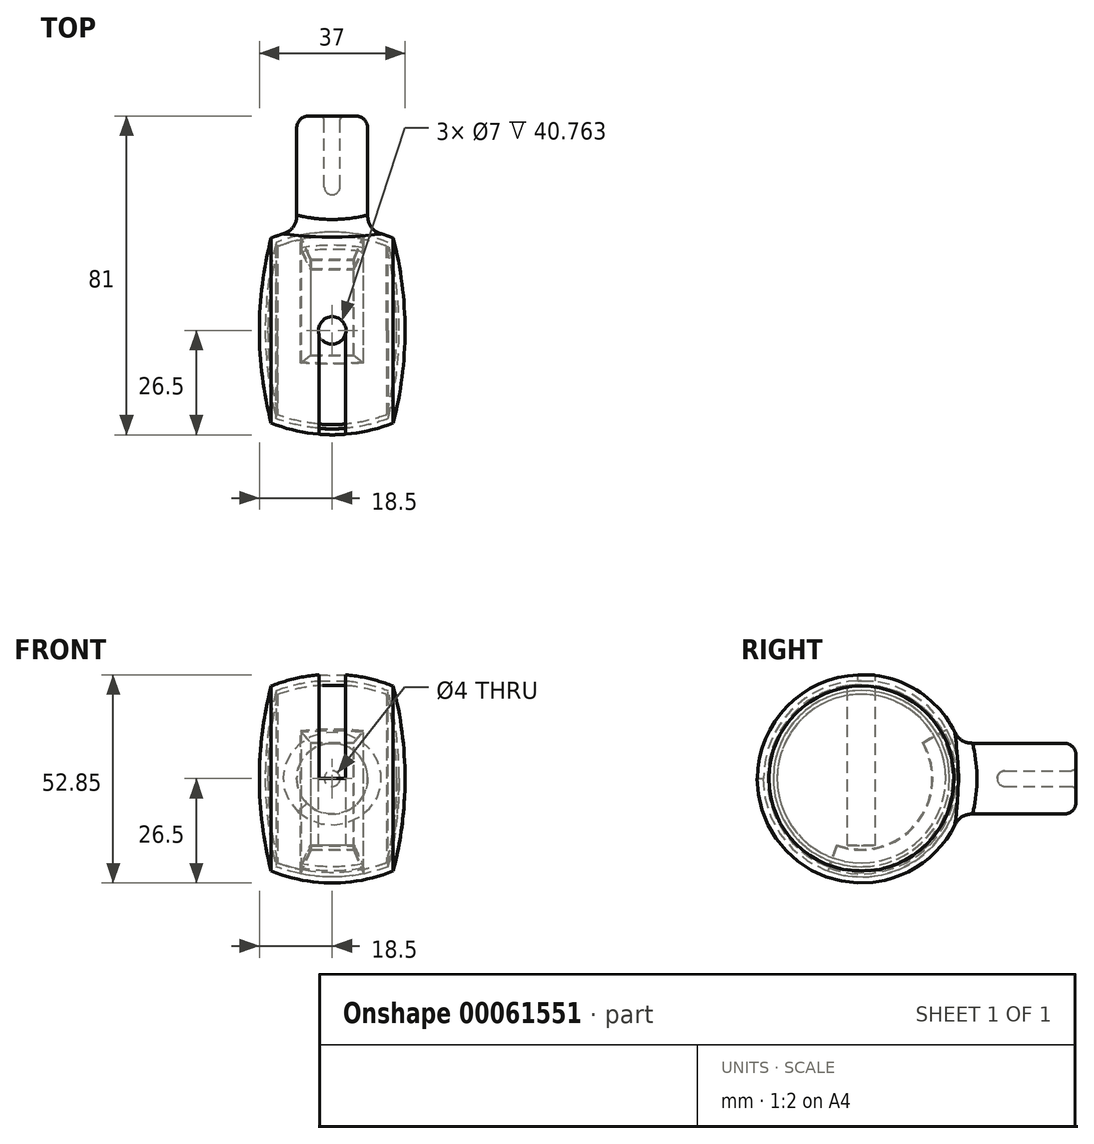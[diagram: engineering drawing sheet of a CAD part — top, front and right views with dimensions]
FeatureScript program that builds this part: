
annotation { "Feature Type Name" : "Feature", "Feature Type Description" : "" }
export const myFeature = defineFeature(function(context is Context, id is Id, definition is map)
    precondition{}
    {
        {
            var Q0;
            Q0=qCreatedBy(makeId("Front.planeOp"),FACE);
            var sketch = newSketch(context, id + "F0", { "sketchPlane" : qUnion([Q0])});
            skLineSegment(sketch, "E0.rect.bottom", {"start": v(18.5, -26.5) * mm, "end": v(-18.5, -26.5) * mm, "construction": true});
            skLineSegment(sketch, "E0.rect.top", {"start": v(18.5, 26.5) * mm, "end": v(-18.5, 26.5) * mm, "construction": true});
            skLineSegment(sketch, "E0.rect.left", {"start": v(18.5, -26.5) * mm, "end": v(18.5, 26.5) * mm, "construction": true});
            skLineSegment(sketch, "E0.rect.right", {"start": v(-18.5, -26.5) * mm, "end": v(-18.5, 26.5) * mm, "construction": true});
            skPoint(sketch, "E0.rect.middle", {"position": v(0, 0) * mm});
            skLineSegment(sketch, "E1.0", {"start": v(15.5, 23.5) * mm, "end": v(-15.5, 23.5) * mm, "construction": true});
            skLineSegment(sketch, "E1.1", {"start": v(15.5, -23.5) * mm, "end": v(15.5, 23.5) * mm, "construction": true});
            skLineSegment(sketch, "E1.2", {"start": v(15.5, -23.5) * mm, "end": v(-15.5, -23.5) * mm, "construction": true});
            skLineSegment(sketch, "E1.3", {"start": v(-15.5, -23.5) * mm, "end": v(-15.5, 23.5) * mm, "construction": true});
            skLineSegment(sketch, "E2", {"start": v(-87, 0) * mm, "end": v(88.34, 0) * mm, "construction": true});
            skArc(sketch, "E3", {"start": v(15.5, 23.5) * mm, "mid": v(0, 26.5) * mm, "end": v(-15.5, 23.5) * mm});
            skArc(sketch, "E4", {"start": v(-15.5, 23.5) * mm, "mid": v(-17.75, 11.85) * mm, "end": v(-18.5, 0) * mm});
            skLineSegment(sketch, "E5", {"start": v(0, 52.42) * mm, "end": v(0, -50.98) * mm, "construction": true});
            skPoint(sketch, "E5.endSnap0", {"position": v(0, -26.5) * mm});
            skArc(sketch, "E6.MirrorCS", {"start": v(15.5, 23.5) * mm, "mid": v(17.75, 11.85) * mm, "end": v(18.5, 0) * mm});
            skPoint(sketch, "E7.orphan", {"position": v(15.5, -23.5) * mm});
            skPoint(sketch, "E8.MirrorCS.center.orphan", {"position": v(0, 30.4) * mm});
            skPoint(sketch, "E8.MirrorCS.end.orphan", {"position": v(-15.5, -23.5) * mm});
            skArc(sketch, "E9.0", {"start": v(-14.24, 22.38) * mm, "mid": v(-16.3, 11.28) * mm, "end": v(-17, 0) * mm});
            skArc(sketch, "E9.1", {"start": v(14.24, 22.38) * mm, "mid": v(0, 25) * mm, "end": v(-14.24, 22.38) * mm});
            skArc(sketch, "E9.2", {"start": v(14.24, 22.38) * mm, "mid": v(16.3, 11.28) * mm, "end": v(17, 0) * mm});
            skLineSegment(sketch, "E10", {"start": v(-18.5, 0) * mm, "end": v(-17, 0) * mm});
            skLineSegment(sketch, "E11", {"start": v(17, 0) * mm, "end": v(18.5, 0) * mm});
            skLineSegment(sketch, "E12", {"start": v(-8.02, 24.19) * mm, "end": v(-5.41, 18.14) * mm});
            skLineSegment(sketch, "E13", {"start": v(-5.41, 18.14) * mm, "end": v(5.41, 18.14) * mm});
            skLineSegment(sketch, "E14", {"start": v(5.41, 18.14) * mm, "end": v(8.02, 24.19) * mm});
            skSolve(sketch);
        }
        {
            var Q0;
            {var subQ0=sQuery(id+"F0.wireOp",EDGE,"E12");Q0=makeQuery(id+"F0.imprint","IMPRINT",FACE,{"disambiguationData":[TD([[makeQuery(id+"F0.imprint","IMPRINT",EDGE,{"derivedFrom":subQ0}),1.0]])]});}
            var Q1;
            Q1=sQuery(id+"F0.wireOp",EDGE,"E2");
            revolve(context, id + "F1", {"entities" : qUnion([Q0]), "axis" : qUnion([Q1]), "revolveType" : RevolveType.ONE_DIRECTION, "oppositeDirection" : true, "angle" : 140 * degree});
        }
        {
            var Q0;
            Q0=qCreatedBy(makeId("Front.planeOp"),FACE);
            var sketch = newSketch(context, id + "F2", { "sketchPlane" : qUnion([Q0])});
            skLineSegment(sketch, "E15.rect.bottom", {"start": v(18.5, -26.5) * mm, "end": v(-18.5, -26.5) * mm, "construction": true});
            skLineSegment(sketch, "E15.rect.top", {"start": v(18.5, 26.5) * mm, "end": v(-18.5, 26.5) * mm, "construction": true});
            skLineSegment(sketch, "E15.rect.left", {"start": v(18.5, -26.5) * mm, "end": v(18.5, 26.5) * mm, "construction": true});
            skLineSegment(sketch, "E15.rect.right", {"start": v(-18.5, -26.5) * mm, "end": v(-18.5, 26.5) * mm, "construction": true});
            skPoint(sketch, "E15.rect.middle", {"position": v(0, 0) * mm});
            skLineSegment(sketch, "E16.0", {"start": v(15.5, 23.5) * mm, "end": v(-15.5, 23.5) * mm, "construction": true});
            skLineSegment(sketch, "E16.1", {"start": v(15.5, -23.5) * mm, "end": v(15.5, 23.5) * mm, "construction": true});
            skLineSegment(sketch, "E16.2", {"start": v(15.5, -23.5) * mm, "end": v(-15.5, -23.5) * mm, "construction": true});
            skLineSegment(sketch, "E16.3", {"start": v(-15.5, -23.5) * mm, "end": v(-15.5, 23.5) * mm, "construction": true});
            skLineSegment(sketch, "E17", {"start": v(-52.75, 0) * mm, "end": v(55.66, 0) * mm, "construction": true});
            skArc(sketch, "E18", {"start": v(15.5, 23.5) * mm, "mid": v(0, 26.5) * mm, "end": v(-15.5, 23.5) * mm});
            skArc(sketch, "E19", {"start": v(-15.5, 23.5) * mm, "mid": v(-17.75, 11.85) * mm, "end": v(-18.5, 0) * mm});
            skLineSegment(sketch, "E20", {"start": v(0, 37.06) * mm, "end": v(0, -36.72) * mm, "construction": true});
            skPoint(sketch, "E20.endSnap0", {"position": v(0, -26.5) * mm});
            skArc(sketch, "E21.MirrorCS", {"start": v(15.5, 23.5) * mm, "mid": v(17.75, 11.85) * mm, "end": v(18.5, 0) * mm});
            skPoint(sketch, "E22.orphan", {"position": v(15.5, -23.5) * mm});
            skPoint(sketch, "E23.MirrorCS.center.orphan", {"position": v(0, 15.04) * mm});
            skPoint(sketch, "E23.MirrorCS.end.orphan", {"position": v(-15.5, -23.5) * mm});
            skArc(sketch, "E24.0", {"start": v(-14.24, 22.38) * mm, "mid": v(-16.3, 11.28) * mm, "end": v(-17, 0) * mm});
            skArc(sketch, "E24.1", {"start": v(14.24, 22.38) * mm, "mid": v(0, 25) * mm, "end": v(-14.24, 22.38) * mm});
            skArc(sketch, "E24.2", {"start": v(14.24, 22.38) * mm, "mid": v(16.3, 11.28) * mm, "end": v(17, 0) * mm});
            skLineSegment(sketch, "E25", {"start": v(17, 0) * mm, "end": v(18.5, 0) * mm});
            skLineSegment(sketch, "E26", {"start": v(-18.5, 0) * mm, "end": v(-17, 0) * mm});
            skSolve(sketch);
        }
        {
            var Q0;
            Q0=qSketchRegion(id+"F2",true);
            var Q1;
            Q1=sQuery(id+"F2.wireOp",EDGE,"E17");
            revolve(context, id + "F3", {"entities" : qUnion([Q0]), "axis" : qUnion([Q1]), "revolveType" : RevolveType.FULL});
        }
        {
            var Q0;
            Q0=makeQuery(id+"F1.opRevolve","SWEPT_BODY",BODY,{"disambiguationData":[OSD([sQuery(id+"F0.wireOp",EDGE,"E9.1"),sQuery(id+"F0.wireOp",EDGE,"E12"),sQuery(id+"F0.wireOp",EDGE,"E13"),sQuery(id+"F0.wireOp",EDGE,"E14")])]});
            var Q1;
            Q1=sQuery(id+"F2.wireOp",EDGE,"E17");
            transform(context, id + "F4", {"entities" : qUnion([Q0]), "transformType" : TransformType.ROTATION, "transformAxis" : qUnion([Q1]), "angle" : 60 * degree, "oppositeDirection" : true, "makeCopy" : false});
        }
        {
            var Q0;
            Q0=qCreatedBy(makeId("Right.planeOp"),FACE);
            var sketch = newSketch(context, id + "F5", { "sketchPlane" : qUnion([Q0])});
            skArc(sketch, "E27", {"start": v(24.92, 9) * mm, "mid": v(26.1, 4.57) * mm, "end": v(26.5, 0) * mm});
            skLineSegment(sketch, "E28.top", {"start": v(24.92, 9) * mm, "end": v(51.5, 9) * mm});
            skLineSegment(sketch, "E28.right", {"start": v(54.5, 3.2) * mm, "end": v(54.5, 6) * mm});
            skLineSegment(sketch, "E29.top", {"start": v(53.3, 2) * mm, "end": v(36.5, 2) * mm});
            skArc(sketch, "E30", {"start": v(36.5, 2) * mm, "mid": v(35.09, 1.41) * mm, "end": v(34.5, 0) * mm});
            skPoint(sketch, "E31.visualSharp", {"position": v(54.5, 2) * mm});
            skArc(sketch, "E31.filletArc", {"start": v(53.3, 2) * mm, "mid": v(54.15, 2.35) * mm, "end": v(54.5, 3.2) * mm});
            skPoint(sketch, "E32.visualSharp", {"position": v(54.5, 9) * mm});
            skArc(sketch, "E32.filletArc", {"start": v(54.5, 6) * mm, "mid": v(53.62, 8.12) * mm, "end": v(51.5, 9) * mm});
            skLineSegment(sketch, "E33", {"start": v(34.5, 0) * mm, "end": v(26.5, 0) * mm});
            skSolve(sketch);
        }
        {
            var Q0;
            Q0=qSketchRegion(id+"F5",true);
            var Q1;
            Q1=sQuery(id+"F5.wireOp",EDGE,"E33");
            revolve(context, id + "F6", {"entities" : qUnion([Q0]), "axis" : qUnion([Q1]), "revolveType" : RevolveType.FULL});
        }
        {
            var Q0;
            Q0=makeQuery(id+"F6.opRevolve","SWEPT_BODY",BODY,{"disambiguationData":[OSD([sQuery(id+"F5.wireOp",EDGE,"E27"),sQuery(id+"F5.wireOp",EDGE,"E28.top"),sQuery(id+"F5.wireOp",EDGE,"E28.right"),sQuery(id+"F5.wireOp",EDGE,"E29.top"),sQuery(id+"F5.wireOp",EDGE,"E30"),sQuery(id+"F5.wireOp",EDGE,"E31.filletArc"),sQuery(id+"F5.wireOp",EDGE,"E32.filletArc"),sQuery(id+"F5.wireOp",EDGE,"E33")])]});
            var Q1;
            Q1=makeQuery(id+"F3.opRevolve","SWEPT_BODY",BODY,{"disambiguationData":[OSD([sQuery(id+"F2.wireOp",EDGE,"E18"),sQuery(id+"F2.wireOp",EDGE,"E19"),sQuery(id+"F2.wireOp",EDGE,"E21.MirrorCS"),sQuery(id+"F2.wireOp",EDGE,"E24.0"),sQuery(id+"F2.wireOp",EDGE,"E24.1"),sQuery(id+"F2.wireOp",EDGE,"E24.2"),sQuery(id+"F2.wireOp",EDGE,"E25"),sQuery(id+"F2.wireOp",EDGE,"E26")])]});
            booleanBodies(context, id + "F7", {"operationType" : BooleanOperationType.UNION, "tools" : qUnion([Q0, Q1])});
        }
        {
            var Q0;
            Q0=makeQuery(id+"F7.opBoolean","INTERSECT",EDGE,{"derivedFrom":[makeQuery(id+"F3.opRevolve","SWEPT_FACE",FACE,{"disambiguationData":[OSD([sQuery(id+"F2.wireOp",EDGE,"E18")])]}),makeQuery(id+"F6.opRevolve","SWEPT_FACE",FACE,{"disambiguationData":[OSD([sQuery(id+"F5.wireOp",EDGE,"E28.top")])]})]});
            fillet(context, id + "F8", {"entities" : qUnion([Q0]), "radius" : 5 * mm, "tangentPropagation" : true, "rho" : 0.5, "crossSection" : FilletCrossSection.CONIC, "allowEdgeOverflow" : false});
        }
        {
            var Q0;
            Q0=qCreatedBy(makeId("Front.planeOp"),FACE);
            var sketch = newSketch(context, id + "F9", { "sketchPlane" : qUnion([Q0])});
            skPoint(sketch, "E34.rect.middle", {"position": v(0, 0) * mm});
            skLineSegment(sketch, "E35", {"start": v(-52.75, 0) * mm, "end": v(55.66, 0) * mm, "construction": true});
            skLineSegment(sketch, "E36", {"start": v(0, 36.48) * mm, "end": v(0, -37.3) * mm, "construction": true});
            skArc(sketch, "E37.0", {"start": v(-13.82, 21.43) * mm, "mid": v(-15.72, 10.79) * mm, "end": v(-16.36, 0) * mm});
            skArc(sketch, "E37.1", {"start": v(13.82, 21.43) * mm, "mid": v(0, 23.92) * mm, "end": v(-13.82, 21.43) * mm});
            skArc(sketch, "E37.2", {"start": v(13.82, 21.43) * mm, "mid": v(15.72, 10.79) * mm, "end": v(16.36, 0) * mm});
            skLineSegment(sketch, "E38", {"start": v(-16.36, 0) * mm, "end": v(16.36, 0) * mm});
            skSolve(sketch);
        }
        {
            var Q0;
            Q0=qSketchRegion(id+"F9",true);
            var Q1;
            Q1=sQuery(id+"F9.wireOp",EDGE,"E35");
            revolve(context, id + "F10", {"entities" : qUnion([Q0]), "axis" : qUnion([Q1]), "revolveType" : RevolveType.FULL});
        }
        {
            var Q0;
            Q0=makeQuery(id+"F10.opRevolve","SWEPT_BODY",BODY,{"disambiguationData":[OSD([sQuery(id+"F9.wireOp",EDGE,"E37.0"),sQuery(id+"F9.wireOp",EDGE,"E37.1"),sQuery(id+"F9.wireOp",EDGE,"E37.2"),sQuery(id+"F9.wireOp",EDGE,"E38")])]});
            transform(context, id + "F11", {"entities" : qUnion([Q0]), "transformType" : TransformType.TRANSLATION_3D, "dx" : 0 * mm, "dy" : 0 * mm, "dz" : 0 * mm, "makeCopy" : true});
        }
        {
            var Q0;
            Q0=makeQuery(id+"F1.opRevolve","SWEPT_BODY",BODY,{"disambiguationData":[OSD([sQuery(id+"F0.wireOp",EDGE,"E9.1"),sQuery(id+"F0.wireOp",EDGE,"E12"),sQuery(id+"F0.wireOp",EDGE,"E13"),sQuery(id+"F0.wireOp",EDGE,"E14")])]});
            var Q1;
            Q1=makeQuery(id+"F11.opPattern","COPY",BODY,{"derivedFrom":makeQuery(id+"F10.opRevolve","SWEPT_BODY",BODY,{"disambiguationData":[OSD([sQuery(id+"F9.wireOp",EDGE,"E37.0"),sQuery(id+"F9.wireOp",EDGE,"E37.1"),sQuery(id+"F9.wireOp",EDGE,"E37.2"),sQuery(id+"F9.wireOp",EDGE,"E38")])]}),"instanceName":"1"});
            booleanBodies(context, id + "F12", {"operationType" : BooleanOperationType.SUBTRACTION, "tools" : qUnion([Q0]), "targets" : qUnion([Q1]), "offset" : true, "offsetAll" : true, "offsetDistance" : 0.2 * mm, "keepTools" : true});
        }
        {
            var Q0;
            Q0=qCreatedBy(makeId("Top.planeOp"),FACE);
            var sketch = newSketch(context, id + "F13", { "sketchPlane" : qUnion([Q0])});
            skCircle(sketch, "E39", {"center": v(0, 0) * mm, "radius": 3.5 * mm});
            skSolve(sketch);
        }
        {
            var Q0;
            Q0=qSketchRegion(id+"F13",true);
            extrude(context, id + "F14", {"entities" : qUnion([Q0]), "operationType" : NewBodyOperationType.REMOVE, "oppositeDirection" : true, "depth" : 17 * mm, "hasSecondDirection" : true, "secondDirectionBound" : BoundingType.THROUGH_ALL, "secondDirectionOppositeDirection" : false, "secondDirectionDepth" : 15 * mm});
        }
        {
            var Q0;
            Q0=qCreatedBy(makeId("Front.planeOp"),FACE);
            var sketch = newSketch(context, id + "F15", { "sketchPlane" : qUnion([Q0])});
            skLineSegment(sketch, "E40.rect.bottom", {"start": v(18.5, -26.5) * mm, "end": v(-18.5, -26.5) * mm, "construction": true});
            skLineSegment(sketch, "E40.rect.top", {"start": v(18.5, 26.5) * mm, "end": v(-18.5, 26.5) * mm, "construction": true});
            skLineSegment(sketch, "E40.rect.left", {"start": v(18.5, -26.5) * mm, "end": v(18.5, 26.5) * mm, "construction": true});
            skLineSegment(sketch, "E40.rect.right", {"start": v(-18.5, -26.5) * mm, "end": v(-18.5, 26.5) * mm, "construction": true});
            skPoint(sketch, "E40.rect.middle", {"position": v(0, 0) * mm});
            skLineSegment(sketch, "E41.0", {"start": v(15.5, 23.5) * mm, "end": v(-15.5, 23.5) * mm, "construction": true});
            skLineSegment(sketch, "E41.1", {"start": v(15.5, -23.5) * mm, "end": v(15.5, 23.5) * mm, "construction": true});
            skLineSegment(sketch, "E41.2", {"start": v(15.5, -23.5) * mm, "end": v(-15.5, -23.5) * mm, "construction": true});
            skLineSegment(sketch, "E41.3", {"start": v(-15.5, -23.5) * mm, "end": v(-15.5, 23.5) * mm, "construction": true});
            skLineSegment(sketch, "E42", {"start": v(-53.46, 0) * mm, "end": v(15.5, 0) * mm, "construction": true});
            skArc(sketch, "E43", {"start": v(3.4, 26.36) * mm, "mid": v(0, 26.5) * mm, "end": v(-3.4, 26.36) * mm});
            skLineSegment(sketch, "E44", {"start": v(0, 36.48) * mm, "end": v(0, -37.3) * mm, "construction": true});
            skPoint(sketch, "E44.endSnap0", {"position": v(0, -26.5) * mm});
            skPoint(sketch, "E45.orphan", {"position": v(15.5, -23.5) * mm});
            skPoint(sketch, "E46.MirrorCS.center.orphan", {"position": v(0, 14.46) * mm});
            skPoint(sketch, "E46.MirrorCS.end.orphan", {"position": v(-15.5, -23.5) * mm});
            skLineSegment(sketch, "E47", {"start": v(3.4, 26.36) * mm, "end": v(3.4, 24.86) * mm});
            skArc(sketch, "E48.trimOffspring", {"start": v(3.4, 24.86) * mm, "mid": v(0, 25) * mm, "end": v(-3.4, 24.86) * mm});
            skLineSegment(sketch, "E49.MirrorCS", {"start": v(-3.4, 26.36) * mm, "end": v(-3.4, 24.86) * mm});
            skPoint(sketch, "E50.MirrorCS.start.orphan", {"position": v(15.5, 23.5) * mm});
            skPoint(sketch, "E51.start.orphan", {"position": v(17.7, 0) * mm});
            skPoint(sketch, "E52.end.orphan", {"position": v(-17.7, 0) * mm});
            skLineSegment(sketch, "E53.trimOffspring", {"start": v(15.5, 0) * mm, "end": v(54.95, 0) * mm, "construction": true});
            skSolve(sketch);
        }
        {
            var Q0;
            Q0=qSketchRegion(id+"F15",true);
            var Q1;
            Q1=sQuery(id+"F15.wireOp",EDGE,"E42");
            revolve(context, id + "F16", {"operationType" : NewBodyOperationType.REMOVE, "entities" : qUnion([Q0]), "axis" : qUnion([Q1]), "revolveType" : RevolveType.ONE_DIRECTION, "angle" : 90 * degree});
        }
        {
            var Q0;
            Q0=makeQuery(id+"F11.opPattern","COPY",BODY,{"derivedFrom":makeQuery(id+"F10.opRevolve","SWEPT_BODY",BODY,{"disambiguationData":[OSD([sQuery(id+"F9.wireOp",EDGE,"E37.0"),sQuery(id+"F9.wireOp",EDGE,"E37.1"),sQuery(id+"F9.wireOp",EDGE,"E37.2"),sQuery(id+"F9.wireOp",EDGE,"E38")])]}),"instanceName":"1"});
            transform(context, id + "F17", {"entities" : qUnion([Q0]), "transformType" : TransformType.TRANSLATION_3D, "dx" : 0 * mm, "dy" : 0 * mm, "dz" : 0 * mm, "makeCopy" : true});
        }
    });
